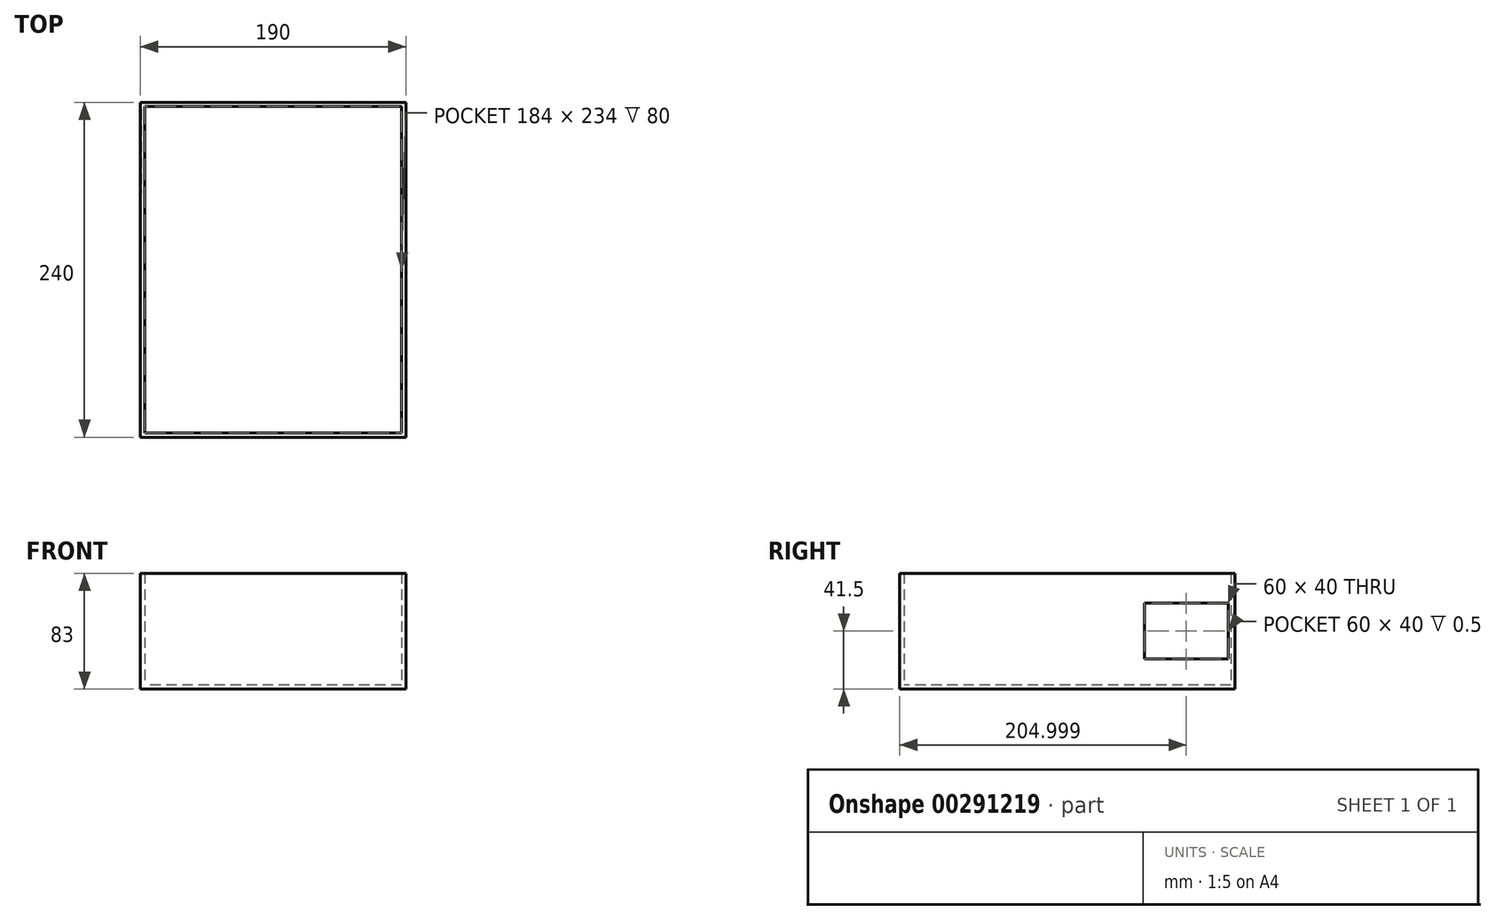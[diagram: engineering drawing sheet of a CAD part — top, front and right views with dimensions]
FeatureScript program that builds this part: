
annotation { "Feature Type Name" : "Feature", "Feature Type Description" : "" }
export const myFeature = defineFeature(function(context is Context, id is Id, definition is map)
    precondition{}
    {
        {
            var Q0;
            Q0=qCreatedBy(makeId("Top.planeOp"),FACE);
            var sketch = newSketch(context, id + "F0", { "sketchPlane" : qUnion([Q0])});
            skLineSegment(sketch, "E0.bottom", {"start": v(-98.86, 76.17) * mm, "end": v(91.14, 76.17) * mm});
            skLineSegment(sketch, "E0.top", {"start": v(-98.86, -163.83) * mm, "end": v(91.14, -163.83) * mm});
            skLineSegment(sketch, "E0.left", {"start": v(-98.86, 76.17) * mm, "end": v(-98.86, -163.83) * mm});
            skLineSegment(sketch, "E0.right", {"start": v(91.14, 76.17) * mm, "end": v(91.14, -163.83) * mm});
            skSolve(sketch);
        }
        {
            var Q0;
            Q0=makeQuery(id+"F0.imprint","IMPRINT",FACE,{"disambiguationData":[TD([[makeQuery(id+"F0.imprint","IMPRINT",EDGE,{"derivedFrom":sQuery(id+"F0.wireOp",EDGE,"E0.bottom")}),-1.0]])]});
            extrude(context, id + "F1", {"entities" : qUnion([Q0]), "depth" : 3 * mm});
        }
        {
            var Q0;
            Q0=makeQuery(id+"F1.opExtrude","CAP_FACE",FACE,{"disambiguationData":[OSD([sQuery(id+"F0.wireOp",EDGE,"E0.bottom"),sQuery(id+"F0.wireOp",EDGE,"E0.top"),sQuery(id+"F0.wireOp",EDGE,"E0.left"),sQuery(id+"F0.wireOp",EDGE,"E0.right")])],"isStart":false});
            var sketch = newSketch(context, id + "F2", { "sketchPlane" : qUnion([Q0])});
            skLineSegment(sketch, "E1.0", {"start": v(-95.86, 73.17) * mm, "end": v(-95.86, -160.83) * mm});
            skLineSegment(sketch, "E1.1", {"start": v(88.14, 73.17) * mm, "end": v(-95.86, 73.17) * mm});
            skLineSegment(sketch, "E1.2", {"start": v(88.14, -160.83) * mm, "end": v(88.14, 73.17) * mm});
            skLineSegment(sketch, "E1.3", {"start": v(-95.86, -160.83) * mm, "end": v(88.14, -160.83) * mm});
            skSolve(sketch);
        }
        {
            var Q0;
            Q0=makeQuery(id+"F2.imprint","IMPRINT",FACE,{"disambiguationData":[TD([[makeQuery(id+"F2.imprint","IMPRINT",EDGE,{"derivedFrom":sQuery(id+"F2.wireOp",EDGE,"E1.0")}),-1.0]])]});
            extrude(context, id + "F3", {"entities" : qUnion([Q0]), "operationType" : NewBodyOperationType.ADD, "depth" : 80 * mm});
        }
        {
            var Q0;
            {var subQ0=sQuery(id+"F0.wireOp",EDGE,"E0.left");Q0=makeQuery(id+"F3.boolean.opBoolean","MERGE",FACE,{"derivedFrom":[makeQuery(id+"F1.opExtrude","SWEPT_FACE",FACE,{"disambiguationData":[OSD([subQ0])]}),makeQuery(id+"F3.opExtrude","SWEPT_FACE",FACE,{"disambiguationData":[OSD([subQ0])]})]});}
            var sketch = newSketch(context, id + "F4", { "sketchPlane" : qUnion([Q0])});
            skLineSegment(sketch, "E2", {"start": v(-76.17, 41.5) * mm, "end": v(-76.17, 61.5) * mm, "construction": true});
            skLineSegment(sketch, "E3", {"start": v(-76.17, 41.5) * mm, "end": v(-76.17, 21.5) * mm, "construction": true});
            skLineSegment(sketch, "E4", {"start": v(-76.17, 41.5) * mm, "end": v(-71.17, 41.5) * mm, "construction": true});
            skLineSegment(sketch, "E5.bottom", {"start": v(-71.17, 21.5) * mm, "end": v(-11.17, 21.5) * mm});
            skLineSegment(sketch, "E5.top", {"start": v(-71.17, 61.5) * mm, "end": v(-11.17, 61.5) * mm});
            skLineSegment(sketch, "E5.left", {"start": v(-71.17, 21.5) * mm, "end": v(-71.17, 61.5) * mm});
            skLineSegment(sketch, "E5.right", {"start": v(-11.17, 21.5) * mm, "end": v(-11.17, 61.5) * mm});
            skSolve(sketch);
        }
        {
            var Q0;
            Q0=makeQuery(id+"F4.imprint","IMPRINT",FACE,{"disambiguationData":[TD([[makeQuery(id+"F4.imprint","IMPRINT",EDGE,{"derivedFrom":sQuery(id+"F4.wireOp",EDGE,"E5.bottom")}),1.0]])]});
            extrude(context, id + "F5", {"entities" : qUnion([Q0]), "operationType" : NewBodyOperationType.REMOVE, "oppositeDirection" : true, "depth" : 0.5 * mm});
        }
        {
            var Q0;
            {var subQ0=sQuery(id+"F0.wireOp",EDGE,"E0.right");Q0=makeQuery(id+"F3.boolean.opBoolean","MERGE",FACE,{"derivedFrom":[makeQuery(id+"F1.opExtrude","SWEPT_FACE",FACE,{"disambiguationData":[OSD([subQ0])]}),makeQuery(id+"F3.opExtrude","SWEPT_FACE",FACE,{"disambiguationData":[OSD([subQ0])]})]});}
            var sketch = newSketch(context, id + "F6", { "sketchPlane" : qUnion([Q0])});
            skLineSegment(sketch, "E6", {"start": v(76.17, 41.5) * mm, "end": v(71.17, 41.5) * mm, "construction": true});
            skLineSegment(sketch, "E7", {"start": v(71.17, 41.5) * mm, "end": v(71.17, 61.5) * mm, "construction": true});
            skLineSegment(sketch, "E8", {"start": v(71.17, 41.5) * mm, "end": v(71.17, 21.5) * mm, "construction": true});
            skLineSegment(sketch, "E9.bottom", {"start": v(71.17, 61.5) * mm, "end": v(11.17, 61.5) * mm});
            skLineSegment(sketch, "E9.top", {"start": v(71.17, 21.5) * mm, "end": v(11.17, 21.5) * mm});
            skLineSegment(sketch, "E9.left", {"start": v(71.17, 61.5) * mm, "end": v(71.17, 21.5) * mm});
            skLineSegment(sketch, "E9.right", {"start": v(11.17, 61.5) * mm, "end": v(11.17, 21.5) * mm});
            skSolve(sketch);
        }
        {
            var Q0;
            Q0=makeQuery(id+"F6.imprint","IMPRINT",FACE,{"disambiguationData":[TD([[makeQuery(id+"F6.imprint","IMPRINT",EDGE,{"derivedFrom":sQuery(id+"F6.wireOp",EDGE,"E9.bottom")}),1.0]])]});
            extrude(context, id + "F7", {"entities" : qUnion([Q0]), "operationType" : NewBodyOperationType.REMOVE, "oppositeDirection" : true, "depth" : 0.5 * mm});
        }
    });
